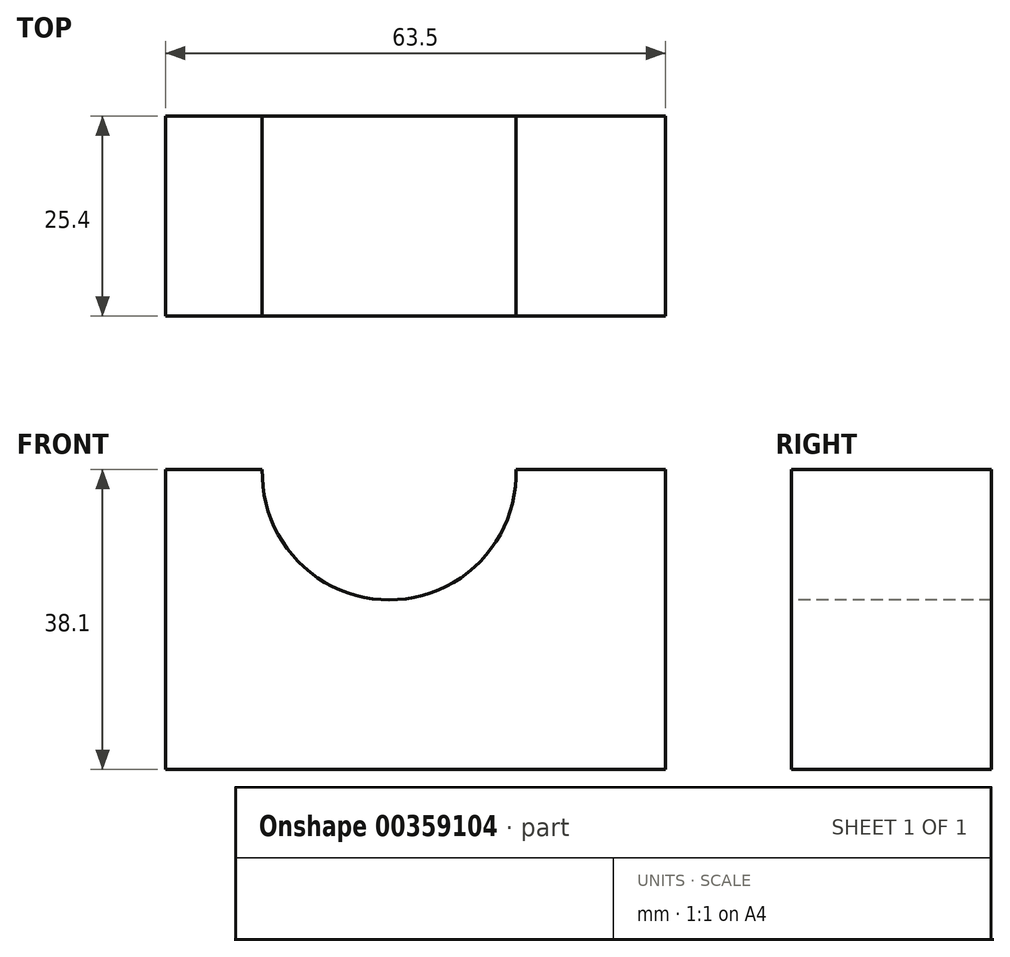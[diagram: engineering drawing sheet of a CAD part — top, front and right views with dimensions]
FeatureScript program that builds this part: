
annotation { "Feature Type Name" : "Feature", "Feature Type Description" : "" }
export const myFeature = defineFeature(function(context is Context, id is Id, definition is map)
    precondition{}
    {
        {
            var Q0;
            Q0=qCreatedBy(makeId("Front.planeOp"),FACE);
            var sketch = newSketch(context, id + "F0", { "sketchPlane" : qUnion([Q0])});
            skLineSegment(sketch, "E0", {"start": v(-69.05, 0) * mm, "end": v(-69.05, 38.1) * mm});
            skLineSegment(sketch, "E1", {"start": v(-69.05, 38.1) * mm, "end": v(-5.55, 38.1) * mm});
            skLineSegment(sketch, "E2", {"start": v(-5.55, 38.1) * mm, "end": v(-5.55, 0) * mm});
            skLineSegment(sketch, "E3", {"start": v(-5.55, 0) * mm, "end": v(-69.05, 0) * mm});
            skSolve(sketch);
        }
        {
            var Q0;
            Q0 = qSketchRegion(id + "F0", true);
            extrude(context, id + "F1", {"entities" : qUnion([Q0]), "depth" : 25.4 * mm});
        }
        {
            var Q0;
            Q0=makeQuery(id+"F1.opExtrude","CAP_FACE",FACE,{"disambiguationData":[OSD([sQuery(id+"F0.wireOp",EDGE,"E0"),sQuery(id+"F0.wireOp",EDGE,"E1"),sQuery(id+"F0.wireOp",EDGE,"E2"),sQuery(id+"F0.wireOp",EDGE,"E3")])],"isStart":false});
            var sketch = newSketch(context, id + "F2", { "sketchPlane" : qUnion([Q0])});
            skArc(sketch, "E4", {"start": v(-56.76, 38.1) * mm, "mid": v(-40.65, 21.53) * mm, "end": v(-24.53, 38.1) * mm});
            skSolve(sketch);
        }
        {
            var Q0;
            {var subQ0=sQuery(id+"F2.wireOp",EDGE,"E4");Q0=makeQuery(id+"F2.imprint","IMPRINT",FACE,{"disambiguationData":[TD([[makeQuery(id+"F2.imprint","IMPRINT",EDGE,{"derivedFrom":subQ0}),1.0]])]});}
            extrude(context, id + "F3", {"entities" : qUnion([Q0]), "operationType" : NewBodyOperationType.REMOVE, "oppositeDirection" : true, "depth" : 25.4 * mm});
        }
    });
